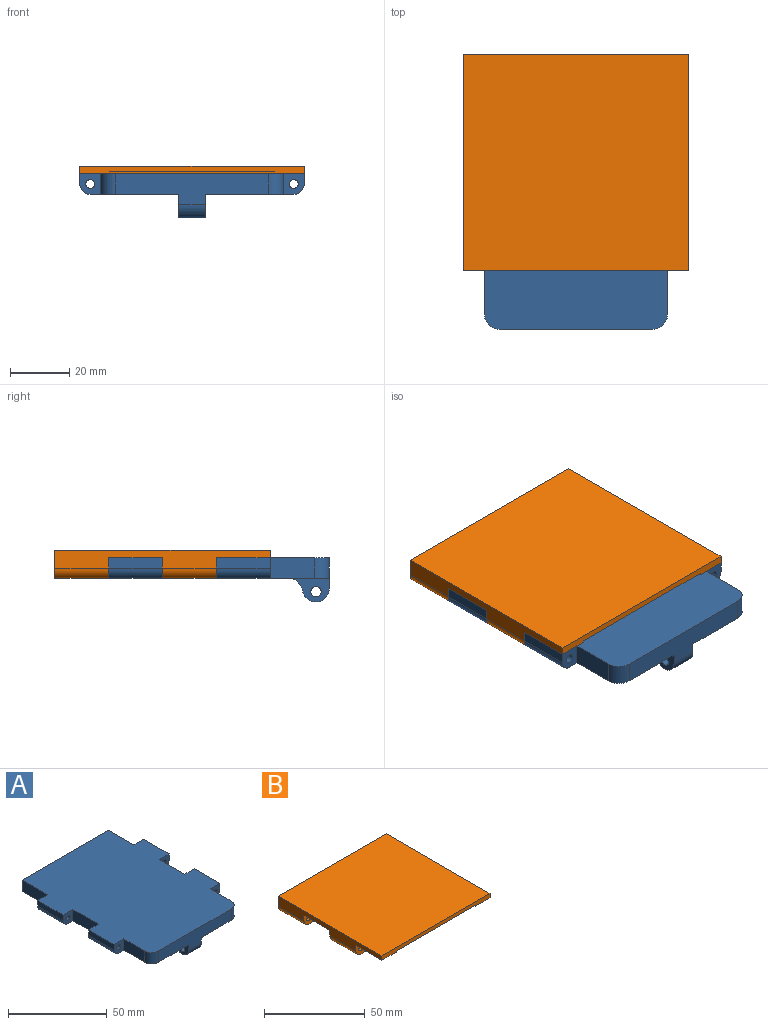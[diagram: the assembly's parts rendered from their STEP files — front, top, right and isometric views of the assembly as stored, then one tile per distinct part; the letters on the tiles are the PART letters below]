
ASSEMBLY  parts=2 mates=1
PART A: 39 faces, bbox 76x93x15 mm
  f0: plane 93x69mm, normal (0,0,-1), area 5884.8mm2, adj f1,f2,f4,f5,f6,f7,f8,f10
  f1: plane 18.25x7mm, normal (1,0,0), area 127.8mm2, adj f0,f2,f20,f21
  f2: plane 7x7mm, normal (0,-1,0), area 39.3mm2, adj f0,f1,f3,f21,f29,f38
  f3: plane 18.25x3.5mm, normal (1,0,0), area 63.9mm2, adj f2,f4,f21,f38
  f4: plane 7x7mm, normal (0,1,0), area 39.3mm2, adj f0,f3,f5,f21,f29,f38
  f5: plane 18.25x7mm, normal (1,0,0), area 127.8mm2, adj f0,f4,f6,f21
  f6: plane 62x7mm, normal (0,1,0), area 434mm2, adj f0,f5,f7,f21
  f7: plane 18.25x7mm, normal (-1,0,0), area 127.8mm2, adj f0,f6,f8,f21
  f8: plane 7x7mm, normal (0,1,0), area 39.3mm2, adj f0,f7,f9,f21,f28,f35
  f9: plane 18.25x3.5mm, normal (-1,0,0), area 63.9mm2, adj f8,f10,f21,f35
  f10: plane 7x7mm, normal (0,-1,0), area 39.3mm2, adj f0,f9,f11,f21,f28,f35
  f11: plane 18.25x7mm, normal (-1,0,0), area 127.8mm2, adj f0,f10,f12,f21
  f12: plane 7x7mm, normal (0,1,0), area 39.3mm2, adj f0,f11,f13,f21,f27,f37
  f13: plane 18.25x3.5mm, normal (-1,0,0), area 63.9mm2, adj f12,f14,f21,f37
  f14: plane 7x7mm, normal (0,-1,0), area 39.3mm2, adj f0,f13,f15,f21,f27,f37
  f15: plane 15x7mm, normal (-1,0,0), area 105mm2, adj f0,f14,f21,f33
  f16: plane 52x10.5mm, normal (0,-1,0), area 395.5mm2, adj f0,f21,f22,f23,f31,f33,f34
  f17: plane 15x7mm, normal (1,0,0), area 105mm2, adj f0,f18,f21,f34
  f18: plane 7x7mm, normal (0,-1,0), area 39.3mm2, adj f0,f17,f19,f21,f26,f36
  f19: plane 18.25x3.5mm, normal (1,0,0), area 63.9mm2, adj f18,f20,f21,f36
  f20: plane 7x7mm, normal (0,1,0), area 39.3mm2, adj f0,f1,f19,f21,f26,f36
  f21: plane 93x76mm, normal (0,0,1), area 6266.3mm2, adj f1,f2,f3,f4,f5,f6,f7,f8
  f22: plane 14x8mm, normal (-1,0,0), area 59.5mm2, adj f0,f16,f24,f25,f30,f31,f32
  f23: plane 14x8mm, normal (1,0,0), area 59.5mm2, adj f0,f16,f24,f25,f30,f31,f32
  f24: plane 9x0.12mm, normal (0,0,-1), area 1.1mm2, adj f22,f23,f31,f32
  f25: cylinder r=1.75mm len=9mm, axis (-1,0,0), area 99mm2, adj f22,f23
  f26: cylinder r=1.5mm len=18.25mm, axis (0,-1,0), area 172mm2, adj f18,f20
  f27: cylinder r=1.5mm len=18.25mm, axis (0,-1,0), area 172mm2, adj f12,f14
  f28: cylinder r=1.5mm len=18.25mm, axis (0,-1,0), area 172mm2, adj f8,f10
  f29: cylinder r=1.5mm len=18.25mm, axis (0,-1,0), area 172mm2, adj f2,f4
  f30: cylinder r=5mm len=9mm, axis (-1,0,0), area 63.6mm2, adj f0,f22,f23,f32
  f31: cylinder r=4.5mm len=9mm, axis (1,0,0), area 63.6mm2, adj f16,f22,f23,f24
  f32: cylinder r=4.5mm len=9mm, axis (-1,0,0), area 57.2mm2, adj f22,f23,f24,f30
  f33: cylinder r=5mm len=7mm, axis (0,0,1), area 55mm2, adj f0,f15,f16,f21
  f34: cylinder r=5mm len=7mm, axis (0,0,-1), area 55mm2, adj f0,f16,f17,f21
  f35: cylinder r=3.5mm len=18.25mm, axis (0,-1,0), area 100.3mm2, adj f0,f8,f9,f10
  f36: cylinder r=3.5mm len=18.25mm, axis (0,1,0), area 100.3mm2, adj f0,f18,f19,f20
  f37: cylinder r=3.5mm len=18.25mm, axis (0,-1,0), area 100.3mm2, adj f0,f12,f13,f14
  f38: cylinder r=3.5mm len=18.25mm, axis (0,1,0), area 100.3mm2, adj f0,f2,f3,f4
PART B: 32 faces, bbox 76x73x9.6 mm
  f0: plane 76x73mm, normal (0,0,-1), area 1229mm2, adj f1,f2,f3,f4,f5,f6,f7,f9
  f1: plane 76x9.6mm, normal (0,1,0), area 276.2mm2, adj f0,f2,f7,f12,f14,f15,f16,f23
  f2: plane 73x6.1mm, normal (-1,0,0), area 317.5mm2, adj f0,f1,f6,f9,f11,f13,f27,f30
  f3: plane 68x0.6mm, normal (1,0,0), area 40.8mm2, adj f0,f4,f6,f26
  f4: plane 56x0.6mm, normal (0,-1,0), area 33.6mm2, adj f0,f3,f5,f26
  f5: plane 68x0.6mm, normal (-1,0,0), area 40.8mm2, adj f0,f4,f6,f26
  f6: plane 76x2.6mm, normal (0,-1,0), area 164mm2, adj f0,f2,f3,f5,f7,f26,f27
  f7: plane 73x6.1mm, normal (1,0,0), area 317.6mm2, adj f0,f1,f6,f17,f19,f21,f27,f28
  f8: plane 18.25x3.5mm, normal (0,0,-1), area 63.9mm2, adj f9,f10,f11,f31
  f9: plane 7x7mm, normal (0,-1,0), area 39.3mm2, adj f0,f2,f8,f10,f25,f31
  f10: plane 18.25x7mm, normal (1,0,0), area 127.8mm2, adj f0,f8,f9,f11
  f11: plane 7x7mm, normal (0,1,0), area 39.3mm2, adj f0,f2,f8,f10,f25,f31
  f12: plane 18.25x3.5mm, normal (0,0,-1), area 63.9mm2, adj f1,f13,f14,f30
  f13: plane 7x7mm, normal (0,-1,0), area 39.3mm2, adj f0,f2,f12,f14,f24,f30
  f14: plane 18.25x7mm, normal (1,0,0), area 127.8mm2, adj f0,f1,f12,f13
  f15: plane 18.25x3.5mm, normal (0,0,-1), area 63.9mm2, adj f1,f16,f17,f28
  f16: plane 18.25x7mm, normal (-1,0,0), area 127.8mm2, adj f0,f1,f15,f17
  f17: plane 7x7mm, normal (0,-1,0), area 39.3mm2, adj f0,f7,f15,f16,f23,f28
  f18: plane 18.25x3.5mm, normal (0,0,-1), area 63.9mm2, adj f19,f20,f21,f29
  f19: plane 7x7mm, normal (0,1,0), area 39.3mm2, adj f0,f7,f18,f20,f22,f29
  f20: plane 18.25x7mm, normal (-1,0,0), area 127.8mm2, adj f0,f18,f19,f21
  f21: plane 7x7mm, normal (0,-1,0), area 39.3mm2, adj f0,f7,f18,f20,f22,f29
  f22: cylinder r=1.5mm len=18.25mm, axis (0,-1,0), area 172mm2, adj f19,f21
  f23: cylinder r=1.5mm len=18.25mm, axis (0,-1,0), area 172mm2, adj f1,f17
  f24: cylinder r=1.5mm len=18.25mm, axis (0,-1,0), area 172mm2, adj f1,f13
  f25: cylinder r=1.5mm len=18.25mm, axis (0,-1,0), area 172mm2, adj f9,f11
  f26: plane 68x56mm, normal (0,0,-1), area 3808mm2, adj f3,f4,f5,f6
  f27: plane 76x73mm, normal (0,0,1), area 5548mm2, adj f1,f2,f6,f7
  f28: cylinder r=3.5mm len=18.25mm, axis (0,1,0), area 100.3mm2, adj f1,f7,f15,f17
  f29: cylinder r=3.5mm len=18.25mm, axis (0,1,0), area 100.3mm2, adj f7,f18,f19,f21
  f30: cylinder r=3.5mm len=18.25mm, axis (0,1,0), area 100.3mm2, adj f1,f2,f12,f13
  f31: cylinder r=3.5mm len=18.25mm, axis (0,1,0), area 100.3mm2, adj f2,f8,f9,f11
PLACE A at identity
PLACE B at identity
MATE fastened A.f27 <-> B.f24  axis (0,-1,0) through (-3.5,56.5,3.5)mm
